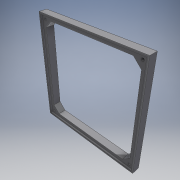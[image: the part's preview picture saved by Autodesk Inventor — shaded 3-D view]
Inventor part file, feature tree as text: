
AUTODESK INVENTOR PART (.ipt)
format: ipt  version: 2018 (Build 220112000, 112)  size: 152,576 bytes
history: native  units: mm
features: extrude x3, sketch x3, other x1
ambient origin geometry x8: Origin, YZ Plane, XZ Plane, XY Plane, X Axis, Y Axis, Z Axis, Center Point
bodies: Body1 (feature_tree)
feature tree (7):
  other  "Těleso1"
  extrude  "Vysunutí1"  Depth=178.0mm
  extrude  "Vysunutí2"  Depth=178.0mm
  extrude  "Vysunutí4"  Depth=9.0mm
  sketch  "Náčrt1"
  sketch  "Náčrt2"
  sketch  "Náčrt3"
